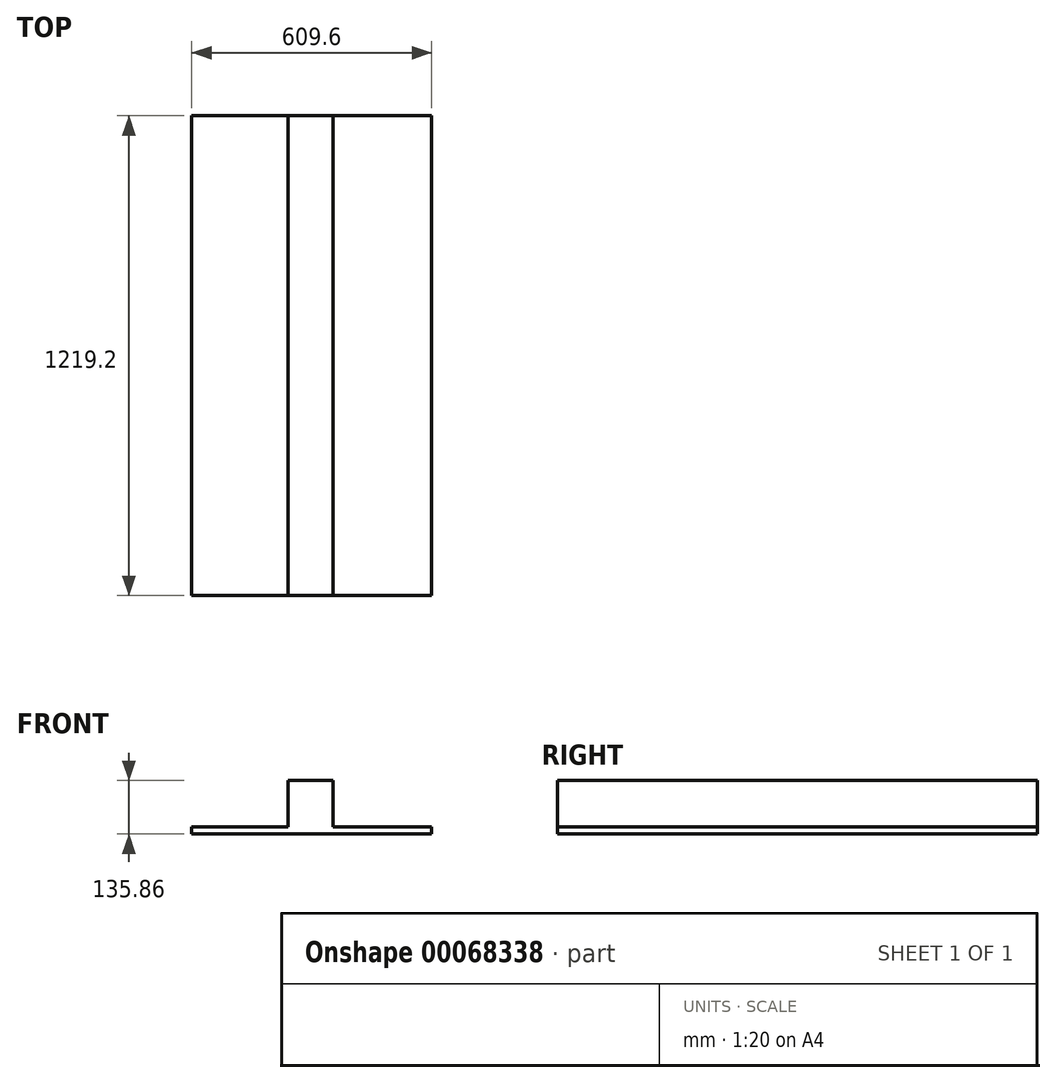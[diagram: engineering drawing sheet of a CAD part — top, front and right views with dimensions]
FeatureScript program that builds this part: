
annotation { "Feature Type Name" : "Feature", "Feature Type Description" : "" }
export const myFeature = defineFeature(function(context is Context, id is Id, definition is map)
    precondition{}
    {
        {
            var Q0;
            Q0=qCreatedBy(makeId("Front.planeOp"),FACE);
            var sketch = newSketch(context, id + "F0", { "sketchPlane" : qUnion([Q0])});
            skLineSegment(sketch, "E0", {"start": v(-304.8, 18.26) * mm, "end": v(304.8, 18.26) * mm});
            skLineSegment(sketch, "E1", {"start": v(304.8, 18.26) * mm, "end": v(-304.8, 18.26) * mm});
            skLineSegment(sketch, "E2", {"start": v(-304.8, -57.94) * mm, "end": v(-304.8, 18.26) * mm});
            skLineSegment(sketch, "E3", {"start": v(-304.8, -57.94) * mm, "end": v(304.8, -57.94) * mm});
            skLineSegment(sketch, "E4", {"start": v(304.8, -57.94) * mm, "end": v(304.8, 18.26) * mm});
            skLineSegment(sketch, "E5", {"start": v(-593.6, -79.2) * mm, "end": v(-304.8, 18.26) * mm});
            skPoint(sketch, "E6.start.orphan", {"position": v(-304.8, -6) * mm});
            skLineSegment(sketch, "E7", {"start": v(-304.8, -57.94) * mm, "end": v(-542.65, -57.94) * mm, "construction": true});
            skLineSegment(sketch, "E8", {"start": v(-304.8, -6) * mm, "end": v(-458.7, -57.94) * mm});
            skLineSegment(sketch, "E9", {"start": v(-458.7, -57.94) * mm, "end": v(-593.6, -79.2) * mm});
            skPoint(sketch, "E10.start.orphan", {"position": v(304.8, -15.68) * mm});
            skLineSegment(sketch, "E11", {"start": v(304.8, 18.26) * mm, "end": v(599.96, -57.8) * mm});
            skLineSegment(sketch, "E12", {"start": v(304.8, 11.9) * mm, "end": v(575.32, -57.8) * mm});
            skLineSegment(sketch, "E13", {"start": v(575.32, -57.8) * mm, "end": v(599.96, -57.8) * mm});
            skLineSegment(sketch, "E14", {"start": v(-60.2, 18.26) * mm, "end": v(-60.2, 135.86) * mm});
            skLineSegment(sketch, "E15", {"start": v(-60.2, 135.86) * mm, "end": v(54.1, 135.86) * mm});
            skLineSegment(sketch, "E16", {"start": v(54.1, 135.86) * mm, "end": v(54.1, 18.26) * mm});
            skLineSegment(sketch, "E17", {"start": v(-304.8, 0) * mm, "end": v(304.8, 0) * mm});
            skSolve(sketch);
        }
        {
            var Q0;
            {var subQ0=sQuery(id+"F0.wireOp",EDGE,"E14");Q0=makeQuery(id+"F0.imprint","IMPRINT",FACE,{"disambiguationData":[TD([[makeQuery(id+"F0.imprint","IMPRINT",EDGE,{"derivedFrom":subQ0}),-1.0]])]});}
            var Q1;
            {var subQ3=sQuery(id+"F0.wireOp",EDGE,"E17");Q1=makeQuery(id+"F0.imprint","IMPRINT",FACE,{"disambiguationData":[TD([[makeQuery(id+"F0.imprint","IMPRINT",EDGE,{"derivedFrom":subQ3}),1.0]])]});}
            extrude(context, id + "F1", {"entities" : qUnion([Q0, Q1]), "endBound" : BoundingType.SYMMETRIC, "depth" : 1219.2 * mm});
        }
    });
